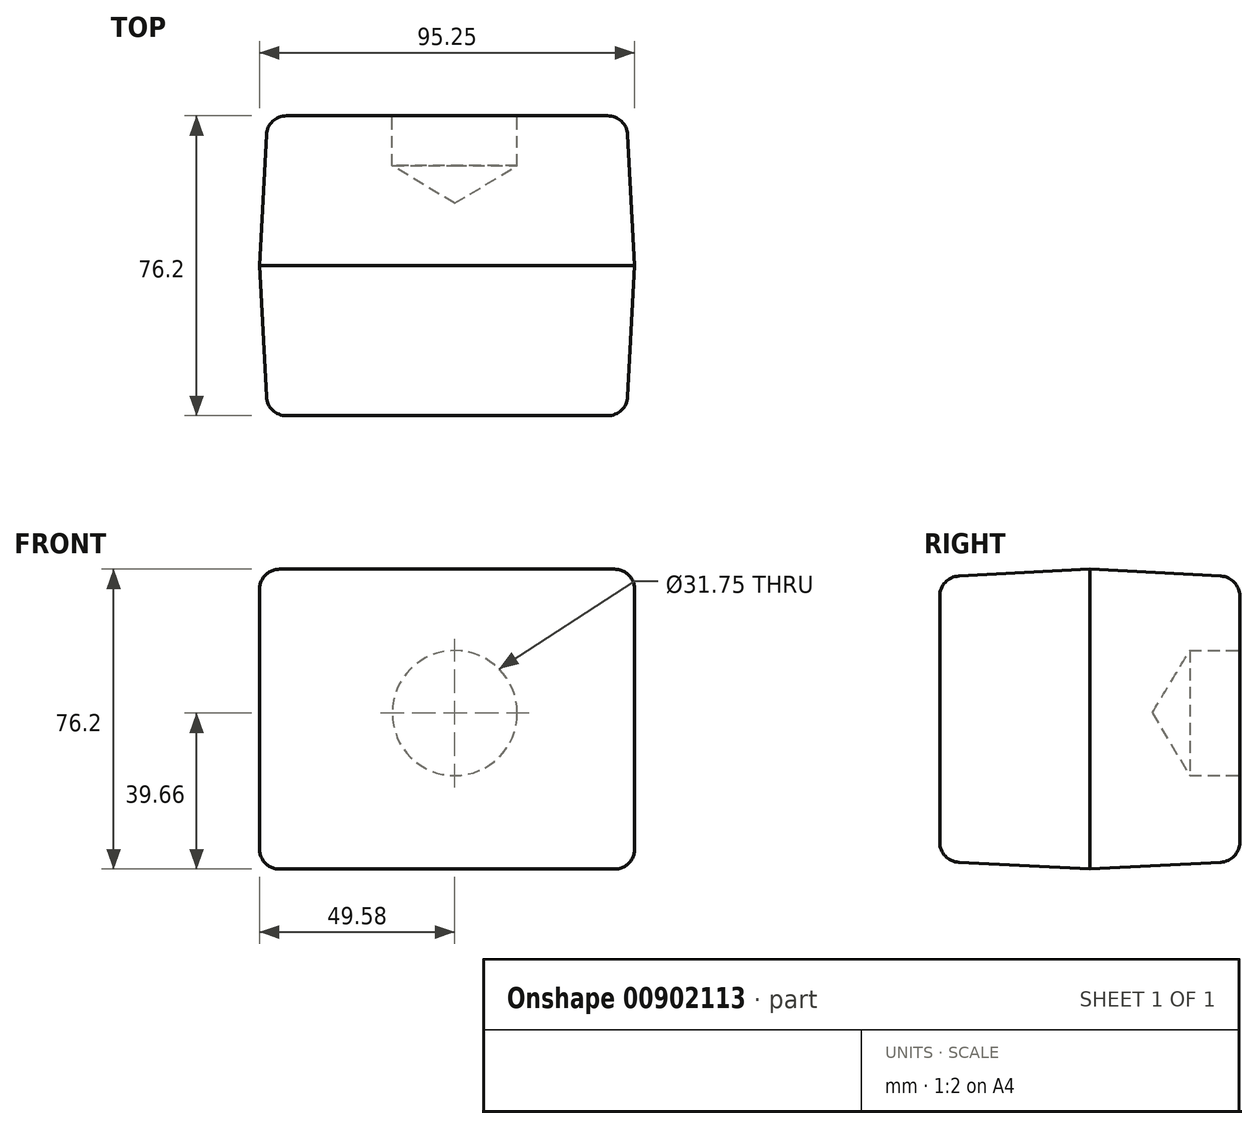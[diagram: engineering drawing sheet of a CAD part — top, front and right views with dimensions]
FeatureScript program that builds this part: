
annotation { "Feature Type Name" : "Feature", "Feature Type Description" : "" }
export const myFeature = defineFeature(function(context is Context, id is Id, definition is map)
    precondition{}
    {
        {
            var Q0;
            Q0=qCreatedBy(makeId("Front.planeOp"),FACE);
            var sketch = newSketch(context, id + "F0", { "sketchPlane" : qUnion([Q0])});
            skLineSegment(sketch, "E0.bottom", {"start": v(-49.58, 36.54) * mm, "end": v(45.67, 36.54) * mm});
            skLineSegment(sketch, "E0.top", {"start": v(-49.58, -39.66) * mm, "end": v(45.67, -39.66) * mm});
            skLineSegment(sketch, "E0.left", {"start": v(-49.58, 36.54) * mm, "end": v(-49.58, -39.66) * mm});
            skLineSegment(sketch, "E0.right", {"start": v(45.67, 36.54) * mm, "end": v(45.67, -39.66) * mm});
            skLineSegment(sketch, "E1", {"start": v(-49.58, -39.66) * mm, "end": v(45.67, 36.54) * mm, "construction": true});
            skSolve(sketch);
        }
        {
            var Q0;
            Q0 = qSketchRegion(id + "F0", true);
            extrude(context, id + "F1", {"entities" : qUnion([Q0]), "endBound" : BoundingType.SYMMETRIC, "depth" : 76.2 * mm, "offsetDistance" : 25.4 * mm, "hasDraft" : true, "draftAngle" : 3 * degree, "draftPullDirection" : true});
        }
        {
            var Q0;
            Q0=makeQuery(id+"F1.*.split.splitOp","SPLIT",EDGE,{"derivedFrom":makeQuery(id+"F1.opExtrude","SWEPT_EDGE",EDGE,{"disambiguationData":[OSD([sQuery(id+"F0.wireOp",EDGE,"E0.bottom"),sQuery(id+"F0.wireOp",EDGE,"E0.left")])]})});
            var Q1;
            Q1=makeQuery(id+"F1.*.split.splitOp","SPLIT",EDGE,{"derivedFrom":makeQuery(id+"F1.opExtrude","SWEPT_EDGE",EDGE,{"disambiguationData":[OSD([sQuery(id+"F0.wireOp",EDGE,"E0.bottom"),sQuery(id+"F0.wireOp",EDGE,"E0.left")])]}),"isFromBackBody":true});
            var Q2;
            Q2=makeQuery(id+"F1.*.split.splitOp","SPLIT",EDGE,{"derivedFrom":makeQuery(id+"F1.opExtrude","SWEPT_EDGE",EDGE,{"disambiguationData":[OSD([sQuery(id+"F0.wireOp",EDGE,"E0.bottom"),sQuery(id+"F0.wireOp",EDGE,"E0.right")])]})});
            var Q3;
            Q3=makeQuery(id+"F1.*.split.splitOp","SPLIT",EDGE,{"derivedFrom":makeQuery(id+"F1.opExtrude","SWEPT_EDGE",EDGE,{"disambiguationData":[OSD([sQuery(id+"F0.wireOp",EDGE,"E0.bottom"),sQuery(id+"F0.wireOp",EDGE,"E0.right")])]}),"isFromBackBody":true});
            var Q4;
            Q4=makeQuery(id+"F1.opExtrude","CAP_FACE",FACE,{"disambiguationData":[OSD([sQuery(id+"F0.wireOp",EDGE,"E0.bottom"),sQuery(id+"F0.wireOp",EDGE,"E0.top"),sQuery(id+"F0.wireOp",EDGE,"E0.left"),sQuery(id+"F0.wireOp",EDGE,"E0.right")])],"isStart":false});
            var Q5;
            Q5=makeQuery(id+"F1.*.split.splitOp","SPLIT",EDGE,{"derivedFrom":makeQuery(id+"F1.opExtrude","SWEPT_EDGE",EDGE,{"disambiguationData":[OSD([sQuery(id+"F0.wireOp",EDGE,"E0.top"),sQuery(id+"F0.wireOp",EDGE,"E0.right")])]})});
            var Q6;
            Q6=makeQuery(id+"F1.*.split.splitOp","SPLIT",EDGE,{"derivedFrom":makeQuery(id+"F1.opExtrude","SWEPT_EDGE",EDGE,{"disambiguationData":[OSD([sQuery(id+"F0.wireOp",EDGE,"E0.top"),sQuery(id+"F0.wireOp",EDGE,"E0.right")])]}),"isFromBackBody":true});
            var Q7;
            Q7=makeQuery(id+"F1.*.split.splitOp","SPLIT",EDGE,{"derivedFrom":makeQuery(id+"F1.opExtrude","SWEPT_EDGE",EDGE,{"disambiguationData":[OSD([sQuery(id+"F0.wireOp",EDGE,"E0.top"),sQuery(id+"F0.wireOp",EDGE,"E0.left")])]})});
            var Q8;
            Q8=makeQuery(id+"F1.*.split.splitOp","SPLIT",EDGE,{"derivedFrom":makeQuery(id+"F1.opExtrude","SWEPT_EDGE",EDGE,{"disambiguationData":[OSD([sQuery(id+"F0.wireOp",EDGE,"E0.top"),sQuery(id+"F0.wireOp",EDGE,"E0.left")])]}),"isFromBackBody":true});
            var Q9;
            Q9=makeQuery(id+"F1.opExtrude","CAP_FACE",FACE,{"disambiguationData":[OSD([sQuery(id+"F0.wireOp",EDGE,"E0.bottom"),sQuery(id+"F0.wireOp",EDGE,"E0.top"),sQuery(id+"F0.wireOp",EDGE,"E0.left"),sQuery(id+"F0.wireOp",EDGE,"E0.right")])],"isStart":true});
            fillet(context, id + "F2", {"entities" : qUnion([Q0, Q1, Q2, Q3, Q4, Q5, Q6, Q7, Q8, Q9]), "radius" : 5.08 * mm, "tangentPropagation" : true, "allowEdgeOverflow" : false});
        }
        {
            var Q0;
            Q0=makeQuery(id+"F1.opExtrude","CAP_FACE",FACE,{"disambiguationData":[OSD([sQuery(id+"F0.wireOp",EDGE,"E0.bottom"),sQuery(id+"F0.wireOp",EDGE,"E0.top"),sQuery(id+"F0.wireOp",EDGE,"E0.left"),sQuery(id+"F0.wireOp",EDGE,"E0.right")])],"isStart":true});
            var sketch = newSketch(context, id + "F3", { "sketchPlane" : qUnion([Q0])});
            skCircle(sketch, "E2", {"center": v(0, 0) * mm, "radius": 15.88 * mm});
            skSolve(sketch);
        }
        {
            var Q0;
            Q0=sQuery(id+"F3.wireOp",VERTEX,"E2.center");
            var Q1;
            Q1=makeQuery(id+"F1.*.split.splitOp","SPLIT",BODY,{"derivedFrom":makeQuery(id+"F1.opExtrude","SWEPT_BODY",BODY,{"disambiguationData":[OSD([sQuery(id+"F0.wireOp",EDGE,"E0.bottom"),sQuery(id+"F0.wireOp",EDGE,"E0.top"),sQuery(id+"F0.wireOp",EDGE,"E0.left"),sQuery(id+"F0.wireOp",EDGE,"E0.right")])]})});
            hole(context, id + "F4", {"style" : HoleStyle.SIMPLE, "endStyle" : HoleEndStyle.BLIND, "holeDiameter" : 31.75 * mm, "majorDiameter" : 6.35 * mm, "holeDepth" : 12.7 * mm, "isTappedThrough" : true, "tappedDepth" : 12.7 * mm, "tapClearance" : 3, "startFromSketch" : true, "locations" : qUnion([Q0]), "scope" : qUnion([Q1])});
        }
    });
